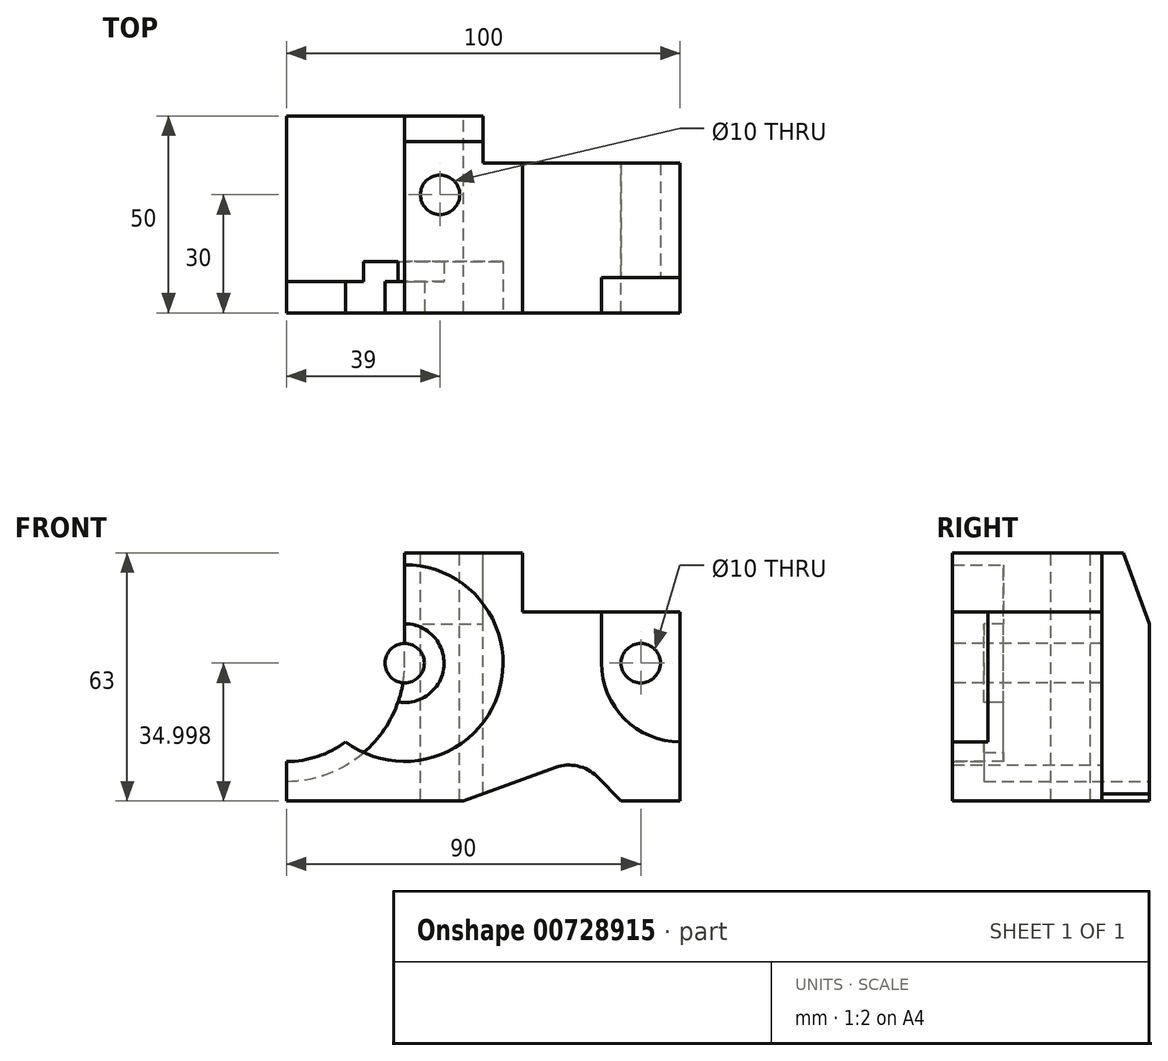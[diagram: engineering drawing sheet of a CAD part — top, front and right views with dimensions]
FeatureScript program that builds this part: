
annotation { "Feature Type Name" : "Feature", "Feature Type Description" : "" }
export const myFeature = defineFeature(function(context is Context, id is Id, definition is map)
    precondition{}
    {
        {
            var Q0;
            Q0=qCreatedBy(makeId("Front.planeOp"),FACE);
            var sketch = newSketch(context, id + "F0", { "sketchPlane" : qUnion([Q0])});
            skLineSegment(sketch, "E0", {"start": v(-29.53, -305.28) * mm, "end": v(30.47, -305.28) * mm});
            skLineSegment(sketch, "E1", {"start": v(-29.53, -305.28) * mm, "end": v(-29.53, -368.28) * mm});
            skLineSegment(sketch, "E2", {"start": v(-29.53, -368.28) * mm, "end": v(15.47, -368.28) * mm});
            skLineSegment(sketch, "E3", {"start": v(70.47, -368.28) * mm, "end": v(70.47, -320.28) * mm});
            skLineSegment(sketch, "E4", {"start": v(15.47, -368.28) * mm, "end": v(38.8, -359.79) * mm});
            skLineSegment(sketch, "E5", {"start": v(55.47, -368.28) * mm, "end": v(49.3, -362.11) * mm});
            skPoint(sketch, "E6.visualSharp", {"position": v(44.8, -357.6) * mm});
            skArc(sketch, "E6.filletArc", {"start": v(49.3, -362.11) * mm, "mid": v(44.4, -359.42) * mm, "end": v(38.8, -359.79) * mm});
            skLineSegment(sketch, "E7.trimOffspring", {"start": v(55.47, -368.28) * mm, "end": v(70.47, -368.28) * mm});
            skLineSegment(sketch, "E8", {"start": v(30.47, -305.28) * mm, "end": v(30.47, -320.28) * mm});
            skLineSegment(sketch, "E9", {"start": v(30.47, -320.28) * mm, "end": v(70.47, -320.28) * mm});
            skSolve(sketch);
        }
        {
            var Q0;
            Q0 = qSketchRegion(id + "F0", true);
            extrude(context, id + "F1", {"entities" : qUnion([Q0]), "depth" : 50 * mm, "offsetDistance" : 25 * mm});
        }
        {
            var Q0;
            Q0=makeQuery(id+"F1.opExtrude","CAP_FACE",FACE,{"disambiguationData":[OSD([sQuery(id+"F0.wireOp",EDGE,"E0"),sQuery(id+"F0.wireOp",EDGE,"E1"),sQuery(id+"F0.wireOp",EDGE,"E2"),sQuery(id+"F0.wireOp",EDGE,"E3"),sQuery(id+"F0.wireOp",EDGE,"E4"),sQuery(id+"F0.wireOp",EDGE,"E5"),sQuery(id+"F0.wireOp",EDGE,"E6.filletArc"),sQuery(id+"F0.wireOp",EDGE,"E7.trimOffspring"),sQuery(id+"F0.wireOp",EDGE,"E8"),sQuery(id+"F0.wireOp",EDGE,"E9")])],"isStart":false});
            var sketch = newSketch(context, id + "F2", { "sketchPlane" : qUnion([Q0])});
            skCircle(sketch, "E10", {"center": v(0.47, -333.28) * mm, "radius": 5 * mm});
            skCircle(sketch, "E11", {"center": v(0.47, -333.28) * mm, "radius": 25 * mm});
            skCircle(sketch, "E12", {"center": v(0.47, -333.28) * mm, "radius": 10 * mm});
            skSolve(sketch);
        }
        {
            var Q0;
            {var subQ0=sQuery(id+"F2.wireOp",EDGE,"E11");var subQ1=makeQuery(id+"F1.opExtrude","CAP_EDGE",EDGE,{"disambiguationData":[OSD([sQuery(id+"F0.wireOp",EDGE,"E1")])],"isStart":false});var subQ2=makeQuery(id+"F2.imprint","INTERSECT",VERTEX,{"disambiguationData":[OD(0.0)],"derivedFrom":[subQ1,subQ0]});Q0=makeQuery(id+"F2.imprint","IMPRINT",FACE,{"disambiguationData":[TD([[makeQuery(id+"F2.imprint","IMPRINT",EDGE,{"disambiguationData":[TD([[subQ2,-1.0]])],"derivedFrom":subQ0}),1.0]])]});}
            var Q1;
            Q1=makeQuery(id+"F2.imprint","IMPRINT",FACE,{"disambiguationData":[TD([[makeQuery(id+"F2.imprint","IMPRINT",EDGE,{"derivedFrom":sQuery(id+"F2.wireOp",EDGE,"E12")}),-1.0]])]});
            extrude(context, id + "F3", {"entities" : qUnion([Q0, Q1]), "operationType" : NewBodyOperationType.REMOVE, "oppositeDirection" : true, "depth" : 13 * mm, "offsetDistance" : 25 * mm});
        }
        {
            var Q0;
            Q0=makeQuery(id+"F2.imprint","IMPRINT",FACE,{"disambiguationData":[TD([[makeQuery(id+"F2.imprint","IMPRINT",EDGE,{"derivedFrom":sQuery(id+"F2.wireOp",EDGE,"E10")}),-1.0]])]});
            extrude(context, id + "F4", {"entities" : qUnion([Q0]), "operationType" : NewBodyOperationType.REMOVE, "oppositeDirection" : true, "depth" : 8 * mm, "offsetDistance" : 25 * mm});
        }
        {
            var Q0;
            Q0=makeQuery(id+"F1.opExtrude","CAP_FACE",FACE,{"disambiguationData":[OSD([sQuery(id+"F0.wireOp",EDGE,"E0"),sQuery(id+"F0.wireOp",EDGE,"E1"),sQuery(id+"F0.wireOp",EDGE,"E2"),sQuery(id+"F0.wireOp",EDGE,"E3"),sQuery(id+"F0.wireOp",EDGE,"E4"),sQuery(id+"F0.wireOp",EDGE,"E5"),sQuery(id+"F0.wireOp",EDGE,"E6.filletArc"),sQuery(id+"F0.wireOp",EDGE,"E7.trimOffspring"),sQuery(id+"F0.wireOp",EDGE,"E8"),sQuery(id+"F0.wireOp",EDGE,"E9")])],"isStart":true});
            var sketch = newSketch(context, id + "F5", { "sketchPlane" : qUnion([Q0])});
            skArc(sketch, "E13", {"start": v(-0.47, -333.28) * mm, "mid": v(54.26, -350.27) * mm, "end": v(18.76, -305.28) * mm});
            skCircle(sketch, "E14", {"center": v(29.53, -333.28) * mm, "radius": 25 * mm});
            skLineSegment(sketch, "E15", {"start": v(-0.47, -333.28) * mm, "end": v(-0.47, -305.28) * mm});
            skLineSegment(sketch, "E16", {"start": v(-0.47, -305.28) * mm, "end": v(29.53, -305.28) * mm});
            skLineSegment(sketch, "E17", {"start": v(29.53, -305.28) * mm, "end": v(29.53, -308.28) * mm});
            skArc(sketch, "E18", {"start": v(-0.05, -338.26) * mm, "mid": v(4.53, -333.07) * mm, "end": v(-0.47, -328.28) * mm});
            skArc(sketch, "E19", {"start": v(9.95, -356) * mm, "mid": v(23.96, -327.95) * mm, "end": v(-0.47, -308.28) * mm});
            skSolve(sketch);
        }
        {
            var Q0;
            {var subQ0=sQuery(id+"F5.wireOp",EDGE,"E14");var subQ1=makeQuery(id+"F1.opExtrude","CAP_EDGE",EDGE,{"disambiguationData":[OSD([sQuery(id+"F0.wireOp",EDGE,"E1")])],"isStart":true});var subQ3=makeQuery(id+"F5.imprint","INTERSECT",VERTEX,{"derivedFrom":[subQ1,subQ0]});Q0=makeQuery(id+"F5.imprint","IMPRINT",FACE,{"disambiguationData":[TD([[makeQuery(id+"F5.imprint","IMPRINT",EDGE,{"disambiguationData":[TD([[subQ3,1.0]])],"derivedFrom":subQ0}),1.0]])]});}
            extrude(context, id + "F6", {"entities" : qUnion([Q0]), "operationType" : NewBodyOperationType.REMOVE, "oppositeDirection" : true, "depth" : 51 * mm, "offsetDistance" : 25 * mm});
        }
        {
            var Q0;
            {var subQ6=sQuery(id+"F5.wireOp",EDGE,"E17");Q0=makeQuery(id+"F5.imprint","IMPRINT",FACE,{"disambiguationData":[TD([[makeQuery(id+"F5.imprint","IMPRINT",EDGE,{"derivedFrom":subQ6}),-1.0]])]});}
            extrude(context, id + "F7", {"entities" : qUnion([Q0]), "operationType" : NewBodyOperationType.REMOVE, "oppositeDirection" : true, "depth" : 51 * mm, "offsetDistance" : 25 * mm});
        }
        {
            var Q0;
            {var subQ0=sQuery(id+"F5.wireOp",EDGE,"E19");var subQ1=sQuery(id+"F5.wireOp",EDGE,"E14");var subQ2=makeQuery(id+"F5.imprint","INTERSECT",VERTEX,{"disambiguationData":[OD(0.0)],"derivedFrom":[subQ1,subQ0]});Q0=makeQuery(id+"F5.imprint","IMPRINT",FACE,{"disambiguationData":[TD([[makeQuery(id+"F5.imprint","IMPRINT",EDGE,{"disambiguationData":[TD([[subQ2,-1.0]])],"derivedFrom":subQ1}),-1.0]])]});}
            extrude(context, id + "F8", {"entities" : qUnion([Q0]), "operationType" : NewBodyOperationType.REMOVE, "oppositeDirection" : true, "depth" : 51 * mm, "offsetDistance" : 25 * mm});
        }
        {
            var Q0;
            {var subQ0=sQuery(id+"F5.wireOp",EDGE,"E14");var subQ3=sQuery(id+"F5.wireOp",EDGE,"E19");var subQ4=makeQuery(id+"F5.imprint","INTERSECT",VERTEX,{"disambiguationData":[OD(0.0)],"derivedFrom":[subQ0,subQ3]});Q0=makeQuery(id+"F5.imprint","IMPRINT",FACE,{"disambiguationData":[TD([[makeQuery(id+"F5.imprint","IMPRINT",EDGE,{"disambiguationData":[TD([[subQ4,1.0]])],"derivedFrom":subQ3}),-1.0]])]});}
            var Q1;
            {var subQ0=sQuery(id+"F5.wireOp",EDGE,"E19");var subQ1=sQuery(id+"F5.wireOp",EDGE,"E14");var subQ6=makeQuery(id+"F5.imprint","INTERSECT",VERTEX,{"disambiguationData":[OD(0.0)],"derivedFrom":[subQ1,subQ0]});Q1=makeQuery(id+"F5.imprint","IMPRINT",FACE,{"disambiguationData":[TD([[makeQuery(id+"F5.imprint","IMPRINT",EDGE,{"disambiguationData":[TD([[subQ6,-1.0]])],"derivedFrom":subQ1}),1.0]])]});}
            extrude(context, id + "F9", {"entities" : qUnion([Q0, Q1]), "operationType" : NewBodyOperationType.REMOVE, "oppositeDirection" : true, "depth" : 51 * mm, "offsetDistance" : 25 * mm});
        }
        {
            var Q0;
            {var subQ0=sQuery(id+"F5.wireOp",EDGE,"E19");var subQ1=sQuery(id+"F5.wireOp",EDGE,"E13");var subQ2=makeQuery(id+"F5.imprint","INTERSECT",VERTEX,{"derivedFrom":[subQ1,subQ0]});Q0=makeQuery(id+"F5.imprint","IMPRINT",FACE,{"disambiguationData":[TD([[makeQuery(id+"F5.imprint","IMPRINT",EDGE,{"disambiguationData":[TD([[subQ2,-1.0]])],"derivedFrom":subQ1}),1.0]])]});}
            extrude(context, id + "F10", {"entities" : qUnion([Q0]), "operationType" : NewBodyOperationType.REMOVE, "oppositeDirection" : true, "depth" : 42 * mm, "offsetDistance" : 25 * mm});
        }
        {
            var Q0;
            {var subQ0=sQuery(id+"F5.wireOp",EDGE,"E18");var subQ1=sQuery(id+"F5.wireOp",EDGE,"E13");var subQ2=makeQuery(id+"F5.imprint","INTERSECT",VERTEX,{"derivedFrom":[subQ1,subQ0]});Q0=makeQuery(id+"F5.imprint","IMPRINT",FACE,{"disambiguationData":[TD([[makeQuery(id+"F5.imprint","IMPRINT",EDGE,{"disambiguationData":[TD([[subQ2,-1.0]])],"derivedFrom":subQ1}),1.0]])]});}
            extrude(context, id + "F11", {"entities" : qUnion([Q0]), "operationType" : NewBodyOperationType.REMOVE, "oppositeDirection" : true, "depth" : 51 * mm, "offsetDistance" : 25 * mm});
        }
        {
            var Q0;
            {var subQ0=sQuery(id+"F5.wireOp",EDGE,"E15");var subQ1=sQuery(id+"F5.wireOp",EDGE,"E13");var subQ2=makeQuery(id+"F5.imprint","INTERSECT",VERTEX,{"derivedFrom":[subQ1,subQ0]});Q0=makeQuery(id+"F5.imprint","IMPRINT",FACE,{"disambiguationData":[TD([[makeQuery(id+"F5.imprint","IMPRINT",EDGE,{"disambiguationData":[TD([[subQ2,-1.0]])],"derivedFrom":subQ1}),1.0]])]});}
            extrude(context, id + "F12", {"entities" : qUnion([Q0]), "operationType" : NewBodyOperationType.REMOVE, "oppositeDirection" : true, "depth" : 42 * mm, "offsetDistance" : 25 * mm});
        }
        {
            var Q0;
            Q0=makeQuery(id+"F1.opExtrude","SWEPT_FACE",FACE,{"disambiguationData":[OSD([sQuery(id+"F0.wireOp",EDGE,"E3")])]});
            var sketch = newSketch(context, id + "F13", { "sketchPlane" : qUnion([Q0])});
            skLineSegment(sketch, "E20", {"start": v(0, -320.28) * mm, "end": v(0, -323.28) * mm});
            skLineSegment(sketch, "E21", {"start": v(0, -323.28) * mm, "end": v(0, -305.28) * mm});
            skLineSegment(sketch, "E22", {"start": v(0, -323.28) * mm, "end": v(-6.55, -305.28) * mm});
            skLineSegment(sketch, "E23", {"start": v(0, -305.28) * mm, "end": v(-6.55, -305.28) * mm});
            skSolve(sketch);
        }
        {
            var Q0;
            Q0 = qSketchRegion(id + "F13", true);
            extrude(context, id + "F14", {"entities" : qUnion([Q0]), "operationType" : NewBodyOperationType.REMOVE, "oppositeDirection" : true, "depth" : 150 * mm, "offsetDistance" : 25 * mm});
        }
        {
            var Q0;
            Q0=makeQuery(id+"F1.opExtrude","SWEPT_FACE",FACE,{"disambiguationData":[OSD([sQuery(id+"F0.wireOp",EDGE,"E0")])]});
            var sketch = newSketch(context, id + "F15", { "sketchPlane" : qUnion([Q0])});
            skLineSegment(sketch, "E24", {"start": v(20.4, 0) * mm, "end": v(71.4, 0) * mm});
            skPoint(sketch, "E25.end.orphan", {"position": v(20.4, 13.7) * mm});
            skLineSegment(sketch, "E26", {"start": v(20.4, 0) * mm, "end": v(20.4, -12) * mm});
            skLineSegment(sketch, "E27", {"start": v(20.4, -12) * mm, "end": v(71.4, -12) * mm});
            skLineSegment(sketch, "E28", {"start": v(71.4, -12) * mm, "end": v(71.4, 0) * mm});
            skSolve(sketch);
        }
        {
            var Q0;
            Q0 = qSketchRegion(id + "F15", true);
            extrude(context, id + "F16", {"entities" : qUnion([Q0]), "operationType" : NewBodyOperationType.REMOVE, "oppositeDirection" : true, "depth" : 100 * mm, "offsetDistance" : 25 * mm});
        }
        {
            var Q0;
            {var subQ0=sQuery(id+"F0.wireOp",EDGE,"E8");var subQ2=sQuery(id+"F0.wireOp",EDGE,"E7.trimOffspring");var subQ4=sQuery(id+"F0.wireOp",EDGE,"E6.filletArc");var subQ6=sQuery(id+"F0.wireOp",EDGE,"E5");var subQ8=sQuery(id+"F0.wireOp",EDGE,"E4");var subQ10=sQuery(id+"F0.wireOp",EDGE,"E9");var subQ12=sQuery(id+"F0.wireOp",EDGE,"E0");var subQ13=makeQuery(id+"F1.opExtrude","SWEPT_FACE",FACE,{"disambiguationData":[OSD([subQ12])]});var subQ14=sQuery(id+"F0.wireOp",EDGE,"E3");var subQ16=sQuery(id+"F0.wireOp",EDGE,"E1");var subQ18=sQuery(id+"F0.wireOp",EDGE,"E2");Q0=makeQuery(id+"F7.boolean.opBoolean","SPLIT",FACE,{"disambiguationData":[TD([subQ13])],"derivedFrom":makeQuery(id+"F3.boolean.opBoolean","SPLIT",FACE,{"disambiguationData":[TD([subQ13])],"derivedFrom":makeQuery(id+"F1.opExtrude","CAP_FACE",FACE,{"disambiguationData":[OSD([subQ12,subQ16,subQ18,subQ14,subQ8,subQ6,subQ4,subQ2,subQ0,subQ10])],"isStart":false})})});}
            var sketch = newSketch(context, id + "F17", { "sketchPlane" : qUnion([Q0])});
            skLineSegment(sketch, "E29", {"start": v(70.47, -368.28) * mm, "end": v(70.47, -333.28) * mm});
            skArc(sketch, "E30", {"start": v(50.47, -333.28) * mm, "mid": v(56.33, -347.42) * mm, "end": v(70.47, -353.28) * mm});
            skLineSegment(sketch, "E31", {"start": v(50.47, -333.28) * mm, "end": v(50.47, -320.28) * mm});
            skLineSegment(sketch, "E32", {"start": v(50.47, -320.28) * mm, "end": v(70.47, -320.28) * mm});
            skLineSegment(sketch, "E33", {"start": v(70.47, -320.28) * mm, "end": v(70.47, -353.28) * mm});
            skSolve(sketch);
        }
        {
            var Q0;
            Q0 = qSketchRegion(id + "F17", true);
            extrude(context, id + "F18", {"entities" : qUnion([Q0]), "operationType" : NewBodyOperationType.REMOVE, "oppositeDirection" : true, "depth" : 9 * mm, "offsetDistance" : 25 * mm});
        }
        {
            var Q0;
            Q0=makeQuery(id+"F18.boolean.opBoolean","COPY",FACE,{"derivedFrom":makeQuery(id+"F18.opExtrude","CAP_FACE",FACE,{"disambiguationData":[OSD([sQuery(id+"F17.wireOp",EDGE,"E30"),sQuery(id+"F17.wireOp",EDGE,"E31"),sQuery(id+"F17.wireOp",EDGE,"E32"),sQuery(id+"F17.wireOp",EDGE,"E33")])],"isStart":false})});
            var sketch = newSketch(context, id + "F19", { "sketchPlane" : qUnion([Q0])});
            skCircle(sketch, "E34", {"center": v(60.47, -333.28) * mm, "radius": 5 * mm});
            skSolve(sketch);
        }
        {
            var Q0;
            Q0 = qSketchRegion(id + "F19", true);
            extrude(context, id + "F20", {"entities" : qUnion([Q0]), "operationType" : NewBodyOperationType.REMOVE, "oppositeDirection" : true, "depth" : 100 * mm, "offsetDistance" : 25 * mm});
        }
        {
            var Q0;
            Q0=makeQuery(id+"F1.opExtrude","SWEPT_FACE",FACE,{"disambiguationData":[OSD([sQuery(id+"F0.wireOp",EDGE,"E0")])]});
            var sketch = newSketch(context, id + "F21", { "sketchPlane" : qUnion([Q0])});
            skLineSegment(sketch, "E35", {"start": v(9.47, -50) * mm, "end": v(9.47, -20) * mm});
            skCircle(sketch, "E36", {"center": v(9.47, -20) * mm, "radius": 5 * mm});
            skSolve(sketch);
        }
        {
            var Q0;
            Q0 = qSketchRegion(id + "F21", true);
            extrude(context, id + "F22", {"entities" : qUnion([Q0]), "operationType" : NewBodyOperationType.REMOVE, "oppositeDirection" : true, "depth" : 100 * mm, "offsetDistance" : 25 * mm});
        }
    });
